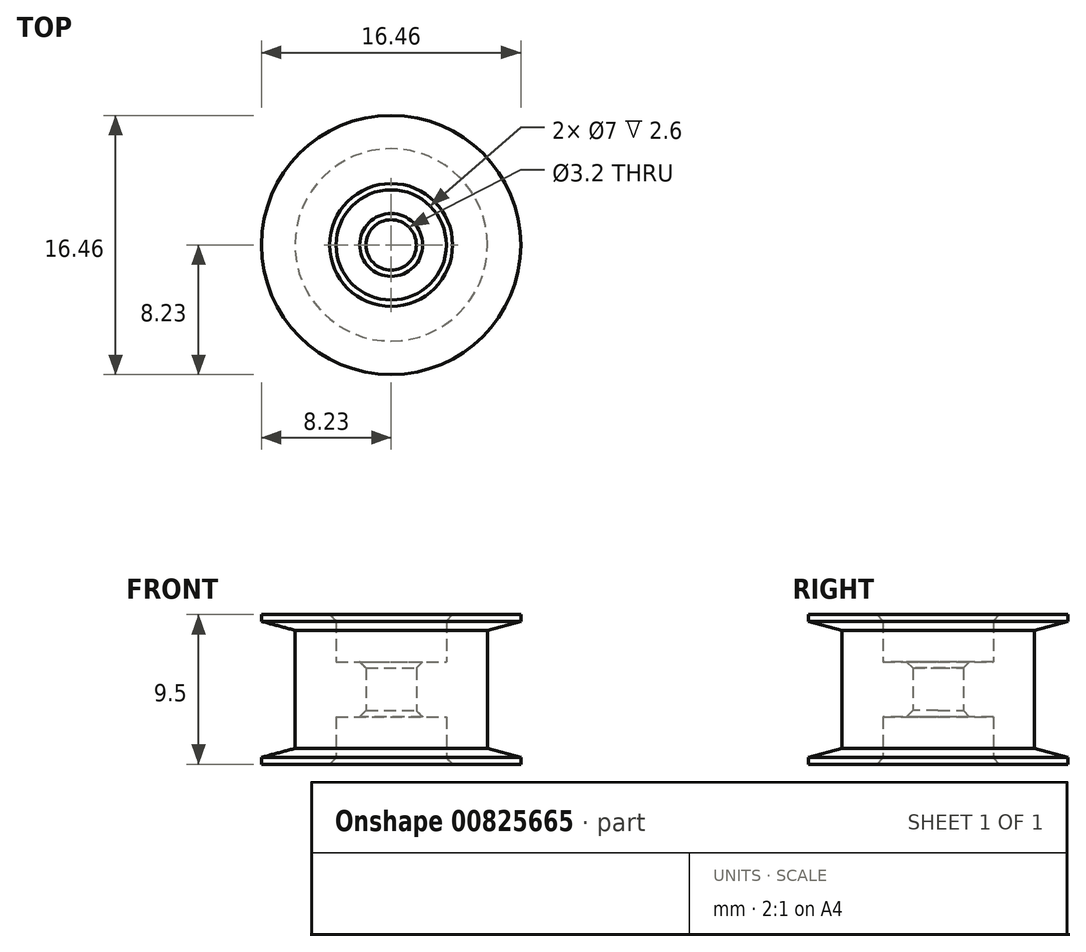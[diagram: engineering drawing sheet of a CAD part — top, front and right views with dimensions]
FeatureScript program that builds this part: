
annotation { "Feature Type Name" : "Feature", "Feature Type Description" : "" }
export const myFeature = defineFeature(function(context is Context, id is Id, definition is map)
    precondition{}
    {
        {
            var Q0;
            Q0=qCreatedBy(makeId("Front.planeOp"),FACE);
            var sketch = newSketch(context, id + "F0", { "sketchPlane" : qUnion([Q0])});
            skLineSegment(sketch, "E0", {"start": v(0, 0) * mm, "end": v(0, 15.15) * mm, "construction": true});
            skLineSegment(sketch, "E1", {"start": v(3.5, 0) * mm, "end": v(3.5, 3) * mm});
            skLineSegment(sketch, "E2", {"start": v(3.5, 3) * mm, "end": v(1.6, 3) * mm});
            skLineSegment(sketch, "E3", {"start": v(1.6, 3) * mm, "end": v(1.6, 6.5) * mm});
            skLineSegment(sketch, "E4", {"start": v(1.6, 6.5) * mm, "end": v(3.5, 6.5) * mm});
            skLineSegment(sketch, "E5", {"start": v(3.5, 6.5) * mm, "end": v(3.5, 9.5) * mm});
            skLineSegment(sketch, "E6", {"start": v(3.5, 9.5) * mm, "end": v(8.23, 9.5) * mm});
            skLineSegment(sketch, "E7", {"start": v(8.23, 9.5) * mm, "end": v(8.23, 9.07) * mm});
            skLineSegment(sketch, "E8", {"start": v(8.23, 9.07) * mm, "end": v(6.11, 8.5) * mm});
            skLineSegment(sketch, "E9", {"start": v(6.11, 8.5) * mm, "end": v(6.11, 1) * mm});
            skLineSegment(sketch, "E10", {"start": v(6.11, 1) * mm, "end": v(8.23, 0.43) * mm});
            skLineSegment(sketch, "E11", {"start": v(8.23, 0.43) * mm, "end": v(8.23, 0) * mm});
            skLineSegment(sketch, "E12", {"start": v(8.23, 0) * mm, "end": v(3.5, 0) * mm});
            skSolve(sketch);
        }
        {
            var Q0;
            Q0=qSketchRegion(id+"F0",true);
            var Q1;
            Q1=sQuery(id+"F0.wireOp",EDGE,"E0");
            revolve(context, id + "F1", {"entities" : qUnion([Q0]), "axis" : qUnion([Q1]), "revolveType" : RevolveType.FULL});
        }
        {
            var Q0;
            Q0=makeQuery(id+"F1.opRevolve","SWEPT_EDGE",EDGE,{"disambiguationData":[OSD([sQuery(id+"F0.wireOp",EDGE,"E5"),sQuery(id+"F0.wireOp",EDGE,"E6")])]});
            var Q1;
            Q1=makeQuery(id+"F1.opRevolve","SWEPT_EDGE",EDGE,{"disambiguationData":[OSD([sQuery(id+"F0.wireOp",EDGE,"E1"),sQuery(id+"F0.wireOp",EDGE,"E12")])]});
            var Q2;
            Q2=makeQuery(id+"F1.opRevolve","SWEPT_FACE",FACE,{"disambiguationData":[OSD([sQuery(id+"F0.wireOp",EDGE,"E3")])]});
            chamfer(context, id + "F2", {"entities" : qUnion([Q0, Q1, Q2]), "width" : 0.4 * mm, "tangentPropagation" : true});
        }
    });
